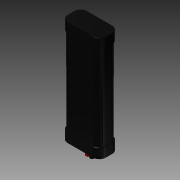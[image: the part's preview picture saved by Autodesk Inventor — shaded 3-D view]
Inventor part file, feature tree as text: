
AUTODESK INVENTOR PART (.ipt)
format: ipt  version: 2015 (Build 190159000, 159)  size: 365,568 bytes
history: native  units: mm
features: fillet x7, extrude x6, sketch x6, other x1
ambient origin geometry x8: Origin, YZ Plane, XZ Plane, XY Plane, X Axis, Y Axis, Z Axis, Center Point
bodies: Body1 (feature_tree)
feature tree (20):
  other  "Sólido1"
  extrude  "Extrusión1"  Depth=105.0mm
  extrude  "Extrusión2"  Depth=47.0mm
  extrude  "Extrusión3"  Depth=24.0mm
  extrude  "Extrusión4"  Depth=8.0mm TaperAngle=0.0deg
  fillet  "Empalme1"  Radius=12.0mm
  fillet  "Empalme2"  Radius=36.0mm
  fillet  "Empalme3"  Radius=5.5mm
  fillet  "Empalme4"  Radius=5.5mm
  fillet  "Empalme5"  Radius=3.0mm
  fillet  "Empalme6"  Radius=8.0mm
  fillet  "Empalme7"  Radius=8.0mm
  extrude  "Extrusión5"  Depth=4.0mm
  extrude  "Extrusión6"  Depth=0.5mm
  sketch  "Boceto1"  dims[d0=45.0mm d1=105.0mm]
  sketch  "Boceto2"  dims[d2=23.0mm d3=0.0mm d4=47.0mm]
  sketch  "Boceto3"  dims[d5=1.0mm d6=24.0mm]
  sketch  "Boceto4"  dims[d8=0.5mm d9=12.0mm d10=0.0mm d11=12.0mm d12=0.0mm d13=36.0mm d14=5.5mm d15=5.5mm d16=3.0mm d17=0.0mm d18=8.0mm d19=8.0mm]
  sketch  "Boceto5"  dims[d20=8.0mm d21=4.0mm]
  sketch  "Boceto6"  dims[d22=0.5mm d23=0.5mm d24=0.5mm d26=5.0mm d29=6.0mm d30=15.0mm d31=9.0mm d32=0.0mm d33=5.0mm d34=5.0mm d35=0.0mm d36=9.0mm d37=0.0mm]
